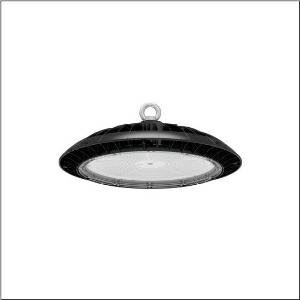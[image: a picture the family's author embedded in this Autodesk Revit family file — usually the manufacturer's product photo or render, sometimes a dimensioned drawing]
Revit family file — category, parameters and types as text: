
# Revit family: highbay_42-l_51hp32mb4mma
name_source: partatom
category: Lighting Fixtures
units: mm (PartAtom-declared; Revit-internal decimal feet)

## family parameters
Cut with Voids When Loaded = No
Host = Face
Light Source = No
Part Type = Normal
Room Calculation Point = No
Round Connector Dimension = Use Diameter
Shared = No

## types (1)
- --- (1 x LED, 28000 lm, 175 W, 4000K)
    Apparent Load = 175 VA
    CIE Flux Codes = 49 82 98 100 100
    Color Rendering = 80
    Color Temperature = 4000K
    Default Elevation = 1800 mm
    Description = Highbay 42-L, high bay luminaire, primary light control with lens, of PC, primary optical cover: cover panel, of PC, transparent, light emission: direct distribution, primary light characteristic: rotationally symmetric, installation type: suspended mounting, surface-mounted, LED, rated luminous flux: 28.000lm, luminous efficacy: 160lm/W, light colour: 840, colour temperature: 4000K, control gear: ON/OFF Multilumen, with cable, 3x 1.0mm², free wire ends, mains connection: 230V, AC, 50Hz, cable length: 1,5m, rated input power: 175W, housing, rotationally symmetric, of diecast aluminium, black, with hook on luminaire side, diameter: 305mm, height: 117mm, protection rating (complete): IP65, insulation class (complete): insulation class I (protective earthing), certification: CE, UKCA, protection symbol: D, impact resistance: IK08, permissible operating ambient temperature: -20..+40°C, corresponds to IFS (International Featured Standards) requirements for safety and quality in the food industry, packaging unit: 1 piece
    Height = 117 mm
    Lamp = 1 x LED
    Lamp Light Flux = 28000 lm
    Lamp Power = 175 W
    Lamp count = 1
    Length = 305 mm
    Luminous efficacy = 160 lm/W
    Manufacturer = Siteco
    ModVariant = No
    Model = 51HP32MB4MMA
    Mounting Place = Ceiling
    Mounting Type = Pendant
    Number of Poles = 1
    OnlyDefault = Yes
    Power Factor = 1
    Product Name = Highbay 42-L
    Product group = high bay luminaire
    ProductGroupID = 901
    Protection Class = Protection class I
    Protection Degree = IP 65
    RLX_Detail_Level = 1
    RLX_Emergency_Light_Flux = 0 lm
    RLX_Emergency_Type = 0
    RLX_Emergency_Type_DB = No
    RlxData = <blob elided: 288033 chars, md5=5da83110>
    Socket = socket
    Standby Power = 0 W
    System Light Flux = 28000 lm
    System Power = 175 W
    Type Comments = factory setting: luminous flux: 100 % | (OFF | OFF | OFF)
    Type Image = l_1003932.jpg
    URL = http://relux.com
    VarID = @adj_218791
    Voltage = 0 V
    Weight = 0.00 kg
    Width = 0 mm  [stored 0 ft]

note: [stored X ft] marks values corroborated as IEEE doubles in the binary element streams (Revit-internal decimal feet)

## geometry (parser evidence)
native form markers: Blend x4, Sweep x12
no freeform markers — native parametric forms only
